# Revit family: Electronics_Conferencing-Cameras_Biamp_Vidi_4K_250__
name_source: partatom
category: Communication Devices
units: mm (PartAtom-declared; Revit-internal decimal feet)

## family parameters
Cut with Voids When Loaded = No
Host = Face
Maintain Annotation Orientation = No
OmniClass Number = 23.85.10.14.11
OmniClass Title = Cameras
Part Type = Normal
Room Calculation Point = No
Round Connector Dimension = Use Diameter
Shared = No

## types (1)
- Vidi 250
    Altitude = 0 - 10,000 ft (0 - 3000m) MSL
    Apparent Load = 10 VA
    Compliance = CE Marked (Europe), UKCA (Great Britain)
    Connector Description = USB-C
    Default Elevation = 48 "
    Depth = 2.8 "
    Description = Vidi™ 250 4K Conferencing Camera
    Diagonal Field of View = 120 Degrees
    Digital Zoom = 5x
    Field Of View Horizontal = 120.00°
    Field Of View Vertical = 120.00°
    Focus Distance Nominal = 100 cm
    Height = 2 "
    Housing Material = Biamp - Plastic - Black
    Humidity = 0-95% relative humidity (non-condensing)
    Image sensor = 12 Megapixel
    Indicators = Camera Active Indicator (White/Off LED)
    Manufacturer = Biamp
    Max Power Consumption = 10 W
    Model = Vidi 250
    Number of Poles = 1
    Positioning = Autoframing capability/Electronic Pan/Tilt/Zoom/UVC controlled
    Power Factor = 1
    Product Documentation Link = https://downloads.biamp.com
    Product Page URL = https://www.biamp.com
    Product data url = https://www.bimobject.com
    Supported Video Resolutions = 720p @ 30fps, 1080p @ 30fps, 2160p @ 30fps
    Temperature Range = 32 - 104° F (0 - 40° C)
    URL = https://www.biamp.com
    USB 3.0 = 1x Type C
    Voltage = 0 V
    Weight = 0.35 lbf
    Width = 2 "

## geometry (parser evidence)
native form markers: Sweep x5
no freeform markers — native parametric forms only
